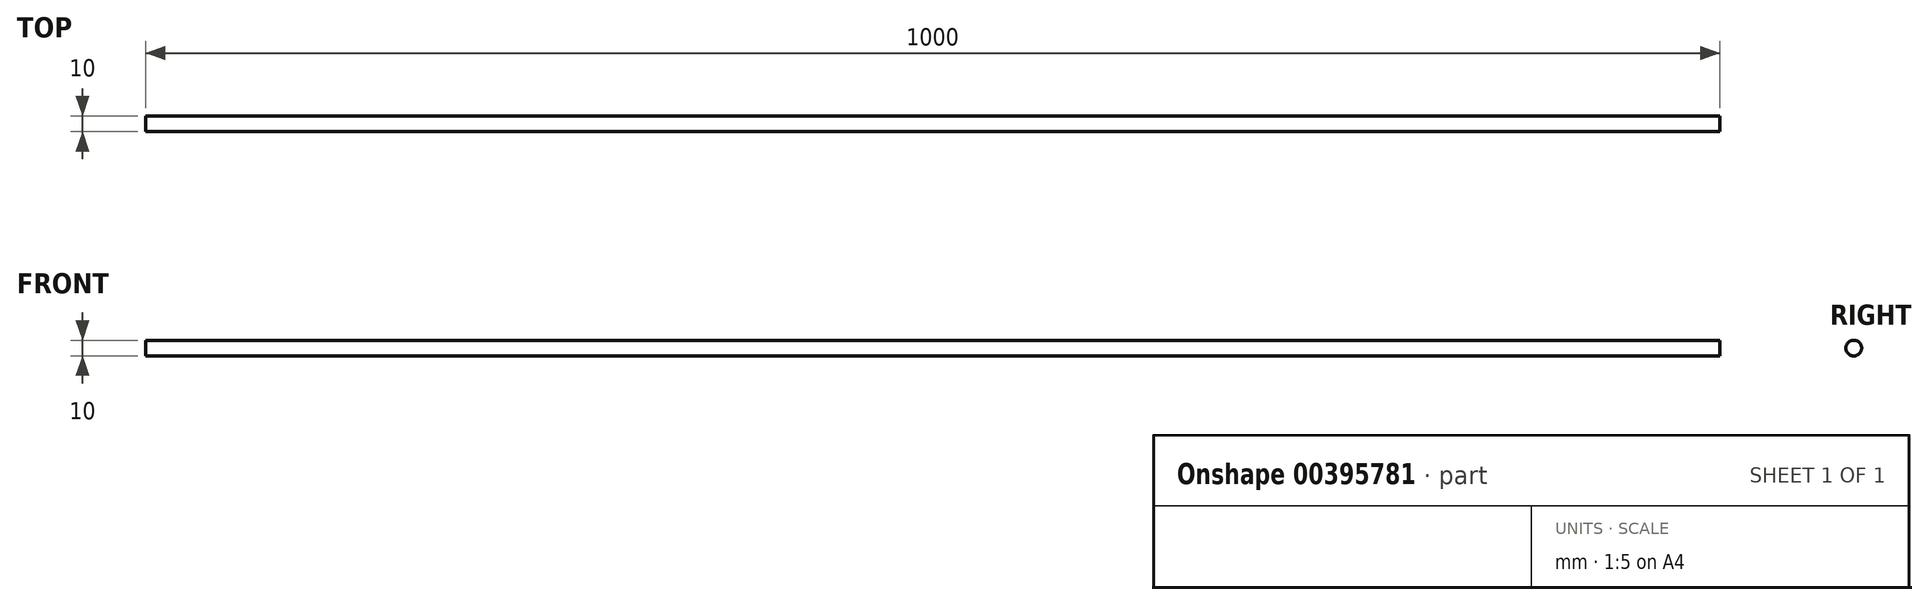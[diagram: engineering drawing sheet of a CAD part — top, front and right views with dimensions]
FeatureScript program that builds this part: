
annotation { "Feature Type Name" : "Feature", "Feature Type Description" : "" }
export const myFeature = defineFeature(function(context is Context, id is Id, definition is map)
    precondition{}
    {
        {
            var Q0;
            Q0=qCreatedBy(makeId("Front.planeOp"),FACE);
            var sketch = newSketch(context, id + "F0", { "sketchPlane" : qUnion([Q0])});
            skLineSegment(sketch, "E0.bottom", {"start": v(0, 0) * mm, "end": v(-1000, 0) * mm});
            skLineSegment(sketch, "E0.top", {"start": v(0, 5) * mm, "end": v(-1000, 5) * mm});
            skLineSegment(sketch, "E0.left", {"start": v(0, 0) * mm, "end": v(0, 5) * mm});
            skLineSegment(sketch, "E0.right", {"start": v(-1000, 0) * mm, "end": v(-1000, 5) * mm});
            skSolve(sketch);
        }
        {
            var Q0;
            Q0 = qSketchRegion(id + "F0", true);
            var Q1;
            Q1=sQuery(id+"F0.wireOp",EDGE,"E0.bottom");
            revolve(context, id + "F1", {"entities" : qUnion([Q0]), "axis" : qUnion([Q1]), "revolveType" : RevolveType.FULL});
        }
    });
